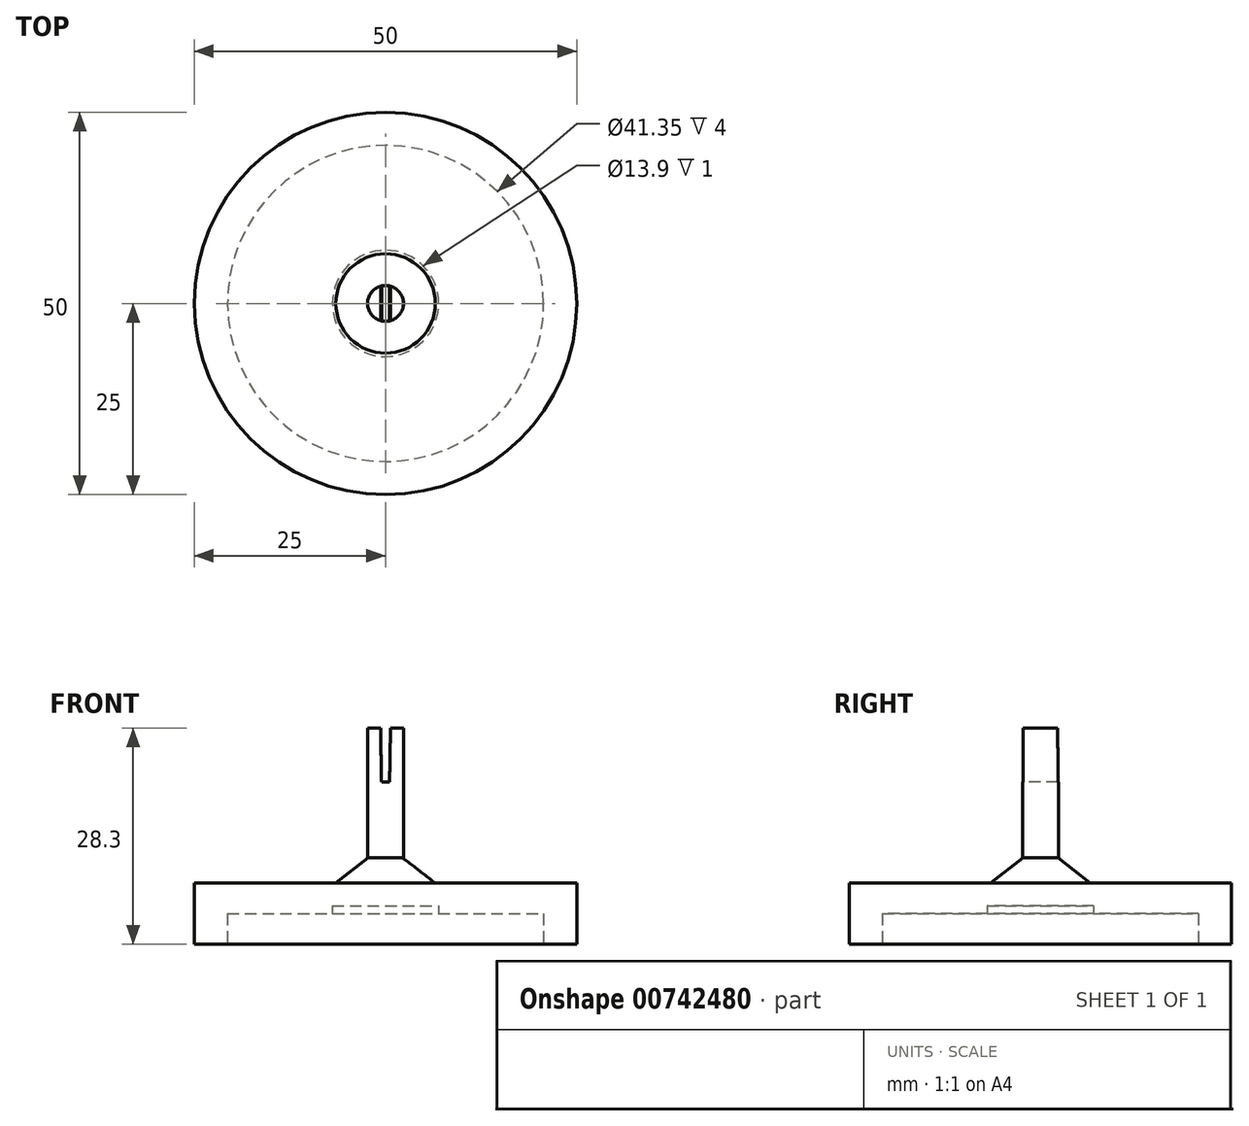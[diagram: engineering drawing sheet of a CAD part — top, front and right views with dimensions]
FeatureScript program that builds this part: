
annotation { "Feature Type Name" : "Feature", "Feature Type Description" : "" }
export const myFeature = defineFeature(function(context is Context, id is Id, definition is map)
    precondition{}
    {
        {
            var Q0;
            Q0=qCreatedBy(makeId("Top.planeOp"),FACE);
            var sketch = newSketch(context, id + "F0", { "sketchPlane" : qUnion([Q0])});
            skCircle(sketch, "E0", {"center": v(0, 0) * mm, "radius": 25 * mm});
            skSolve(sketch);
        }
        {
            var Q0;
            Q0=qSketchRegion(id+"F0",true);
            extrude(context, id + "F1", {"entities" : qUnion([Q0]), "depth" : 8 * mm, "offsetDistance" : 25 * mm});
        }
        {
            var Q0;
            Q0=makeQuery(id+"F1.opExtrude","CAP_FACE",FACE,{"disambiguationData":[OSD([sQuery(id+"F0.wireOp",EDGE,"E0")])],"isStart":true});
            var sketch = newSketch(context, id + "F2", { "sketchPlane" : qUnion([Q0])});
            skCircle(sketch, "E1", {"center": v(0, 0) * mm, "radius": 20.68 * mm});
            skSolve(sketch);
        }
        {
            var Q0;
            Q0=makeQuery(id+"F2.imprint","IMPRINT",FACE,{"disambiguationData":[TD([[makeQuery(id+"F2.imprint","IMPRINT",EDGE,{"derivedFrom":sQuery(id+"F2.wireOp",EDGE,"E1")}),1.0]])]});
            extrude(context, id + "F3", {"entities" : qUnion([Q0]), "operationType" : NewBodyOperationType.REMOVE, "oppositeDirection" : true, "depth" : 4 * mm, "offsetDistance" : 25 * mm});
        }
        {
            var Q0;
            Q0=makeQuery(id+"F3.boolean.opBoolean","COPY",FACE,{"derivedFrom":makeQuery(id+"F3.opExtrude","CAP_FACE",FACE,{"disambiguationData":[OSD([sQuery(id+"F2.wireOp",EDGE,"E1")])],"isStart":false})});
            var sketch = newSketch(context, id + "F4", { "sketchPlane" : qUnion([Q0])});
            skCircle(sketch, "E2", {"center": v(0, 0) * mm, "radius": 6.95 * mm});
            skSolve(sketch);
        }
        {
            var Q0;
            Q0=qSketchRegion(id+"F4",true);
            extrude(context, id + "F5", {"entities" : qUnion([Q0]), "operationType" : NewBodyOperationType.REMOVE, "oppositeDirection" : true, "depth" : 1 * mm, "offsetDistance" : 25 * mm});
        }
        {
            var Q0;
            Q0=makeQuery(id+"F1.opExtrude","CAP_FACE",FACE,{"disambiguationData":[OSD([sQuery(id+"F0.wireOp",EDGE,"E0")])],"isStart":false});
            var sketch = newSketch(context, id + "F6", { "sketchPlane" : qUnion([Q0])});
            skCircle(sketch, "E3", {"center": v(0, 0) * mm, "radius": 6.5 * mm});
            skSolve(sketch);
        }
        {
            var Q0;
            Q0=makeQuery(id+"F6.imprint","IMPRINT",FACE,{"disambiguationData":[TD([[makeQuery(id+"F6.imprint","IMPRINT",EDGE,{"derivedFrom":sQuery(id+"F6.wireOp",EDGE,"E3")}),1.0]])]});
            var Q1;
            Q1=qSketchRegion(id+"F12",true);
            extrude(context, id + "F7", {"entities" : qUnion([Q0, Q1]), "operationType" : NewBodyOperationType.ADD, "depth" : 3.3 * mm, "offsetDistance" : 25 * mm, "hasDraft" : true, "draftAngle" : 52 * degree, "draftPullDirection" : true});
        }
        {
            var Q0;
            Q0=makeQuery(id+"F7.opExtrude","CAP_FACE",FACE,{"disambiguationData":[OSD([sQuery(id+"F6.wireOp",EDGE,"E3")])],"isStart":false});
            var sketch = newSketch(context, id + "F8", { "sketchPlane" : qUnion([Q0])});
            skCircle(sketch, "E4", {"center": v(0, 0) * mm, "radius": 2.35 * mm});
            skSolve(sketch);
        }
        {
            var Q0;
            Q0=qSketchRegion(id+"F8",true);
            extrude(context, id + "F9", {"entities" : qUnion([Q0]), "operationType" : NewBodyOperationType.ADD, "depth" : 17 * mm, "offsetDistance" : 25 * mm});
        }
        {
            var Q0;
            Q0=makeQuery(id+"F9.opExtrude","CAP_FACE",FACE,{"disambiguationData":[OSD([sQuery(id+"F8.wireOp",EDGE,"E4")])],"isStart":false});
            var sketch = newSketch(context, id + "F10", { "sketchPlane" : qUnion([Q0])});
            skLineSegment(sketch, "E5.bottom", {"start": v(0.65, -4) * mm, "end": v(-0.65, -4) * mm});
            skLineSegment(sketch, "E5.top", {"start": v(0.65, 4) * mm, "end": v(-0.65, 4) * mm});
            skLineSegment(sketch, "E5.left", {"start": v(0.65, -4) * mm, "end": v(0.65, 4) * mm});
            skLineSegment(sketch, "E5.right", {"start": v(-0.65, -4) * mm, "end": v(-0.65, 4) * mm});
            skPoint(sketch, "E5.middle", {"position": v(0, 0) * mm});
            skSolve(sketch);
        }
        {
            var Q0;
            {var subQ0=sQuery(id+"F10.wireOp",EDGE,"E5.top");Q0=makeQuery(id+"F10.imprint","IMPRINT",FACE,{"disambiguationData":[TD([[makeQuery(id+"F10.imprint","IMPRINT",EDGE,{"derivedFrom":subQ0}),1.0]])]});}
            var Q1;
            {var subQ0=sQuery(id+"F10.wireOp",EDGE,"E5.left");var subQ1=makeQuery(id+"F9.opExtrude","CAP_EDGE",EDGE,{"disambiguationData":[OSD([sQuery(id+"F8.wireOp",EDGE,"E4")])],"isStart":false});var subQ2=makeQuery(id+"F10.imprint","INTERSECT",VERTEX,{"disambiguationData":[OD(0.0)],"derivedFrom":[subQ1,subQ0]});Q1=makeQuery(id+"F10.imprint","IMPRINT",FACE,{"disambiguationData":[TD([[makeQuery(id+"F10.imprint","IMPRINT",EDGE,{"disambiguationData":[TD([[subQ2,-1.0]])],"derivedFrom":subQ0}),1.0]])]});}
            var Q2;
            {var subQ0=sQuery(id+"F10.wireOp",EDGE,"E5.bottom");Q2=makeQuery(id+"F10.imprint","IMPRINT",FACE,{"disambiguationData":[TD([[makeQuery(id+"F10.imprint","IMPRINT",EDGE,{"derivedFrom":subQ0}),-1.0]])]});}
            extrude(context, id + "F11", {"entities" : qUnion([Q0, Q1, Q2]), "operationType" : NewBodyOperationType.REMOVE, "oppositeDirection" : true, "depth" : 7.1 * mm, "offsetDistance" : 25 * mm, "hasDraft" : true, "draftAngle" : 1 * degree, "draftPullDirection" : true});
        }
    });
